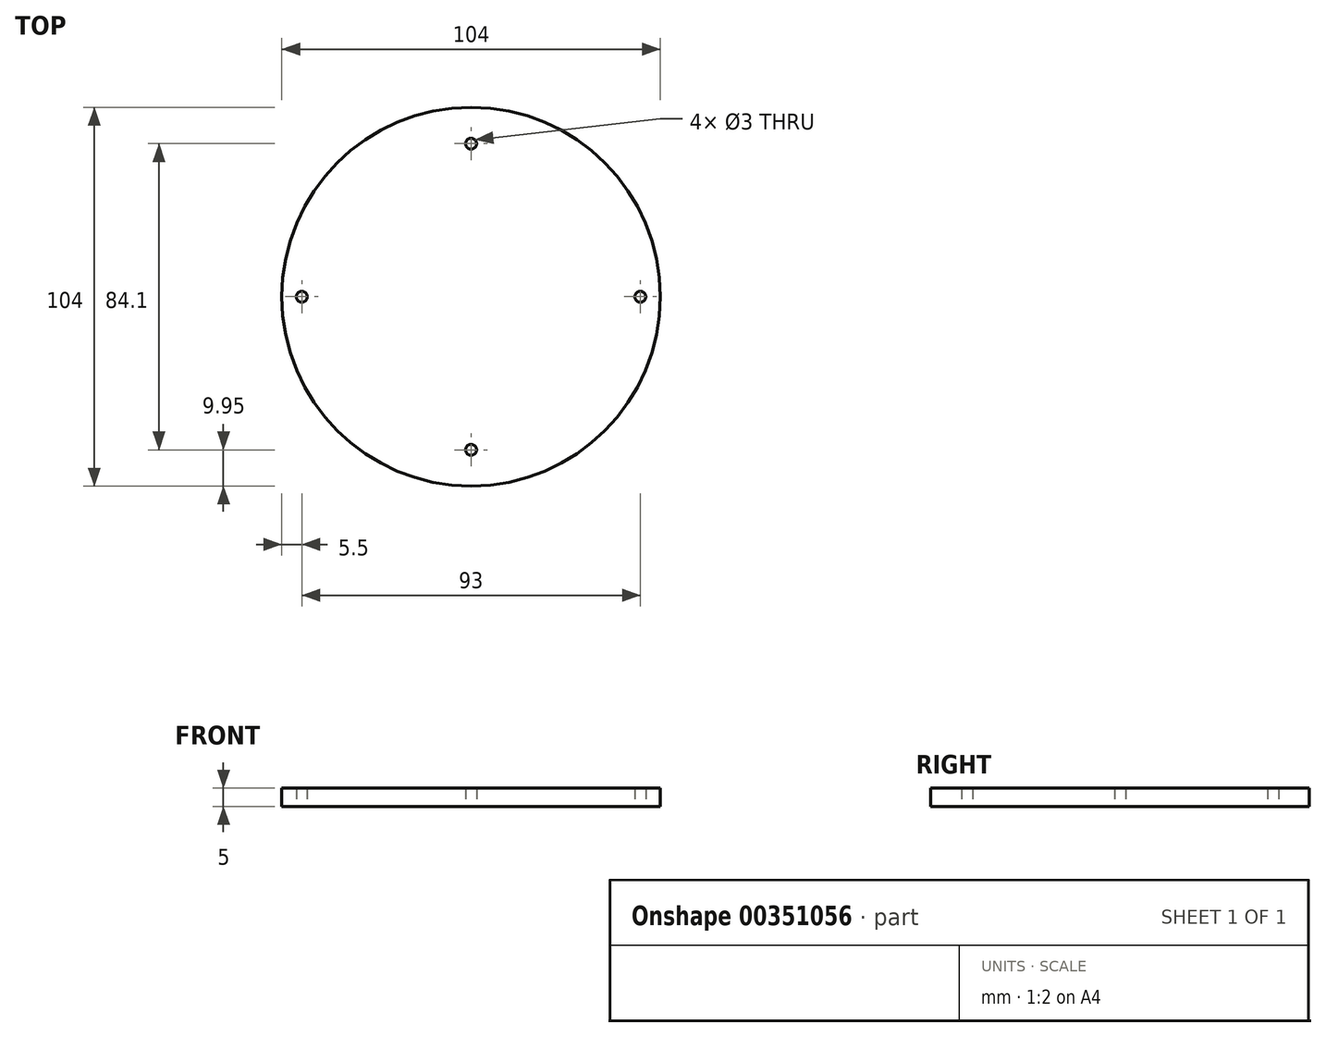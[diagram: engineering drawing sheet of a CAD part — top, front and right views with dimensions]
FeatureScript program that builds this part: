
annotation { "Feature Type Name" : "Feature", "Feature Type Description" : "" }
export const myFeature = defineFeature(function(context is Context, id is Id, definition is map)
    precondition{}
    {
        {
            var Q0;
            Q0=qCreatedBy(makeId("Top.planeOp"),FACE);
            var sketch = newSketch(context, id + "F0", { "sketchPlane" : qUnion([Q0])});
            skCircle(sketch, "E0", {"center": v(0, 0) * mm, "radius": 52 * mm});
            skCircle(sketch, "E1", {"center": v(46.5, 0) * mm, "radius": 1.5 * mm});
            skCircle(sketch, "E2.MirrorC", {"center": v(-46.5, 0) * mm, "radius": 1.5 * mm});
            skCircle(sketch, "E3", {"center": v(0, 42.05) * mm, "radius": 1.5 * mm});
            skCircle(sketch, "E4.MirrorC", {"center": v(0, -42.05) * mm, "radius": 1.5 * mm});
            skSolve(sketch);
        }
        {
            var Q0;
            Q0=makeQuery(id+"F0.imprint","IMPRINT",FACE,{"disambiguationData":[TD([[makeQuery(id+"F0.imprint","IMPRINT",EDGE,{"derivedFrom":sQuery(id+"F0.wireOp",EDGE,"E0")}),1.0]])]});
            extrude(context, id + "F1", {"entities" : qUnion([Q0]), "depth" : 5 * mm});
        }
    });
